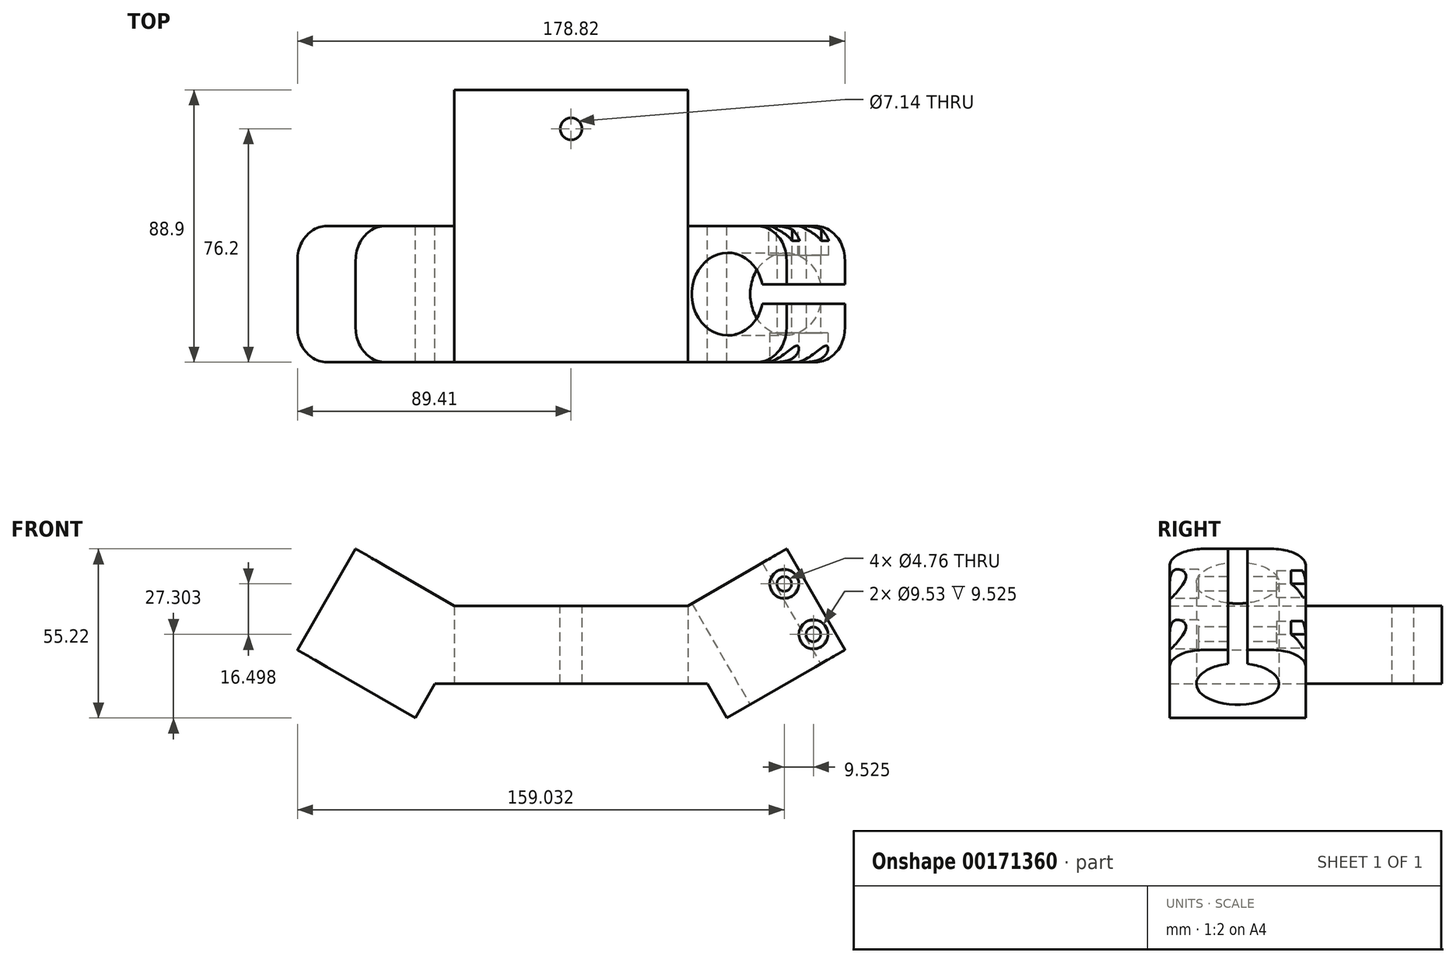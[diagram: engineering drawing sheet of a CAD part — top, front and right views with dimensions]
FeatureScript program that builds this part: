
annotation { "Feature Type Name" : "Feature", "Feature Type Description" : "" }
export const myFeature = defineFeature(function(context is Context, id is Id, definition is map)
    precondition{}
    {
        {
            var Q0;
            Q0=qCreatedBy(makeId("Front.planeOp"),FACE);
            var sketch = newSketch(context, id + "F0", { "sketchPlane" : qUnion([Q0])});
            skLineSegment(sketch, "E0", {"start": v(0, 0) * mm, "end": v(38.1, 0) * mm});
            skLineSegment(sketch, "E1", {"start": v(38.1, 0) * mm, "end": v(70.36, 18.62) * mm});
            skLineSegment(sketch, "E2", {"start": v(70.36, 18.62) * mm, "end": v(89.4, -14.37) * mm});
            skLineSegment(sketch, "E3", {"start": v(89.4, -14.37) * mm, "end": v(50.91, -36.6) * mm});
            skLineSegment(sketch, "E4", {"start": v(50.91, -36.6) * mm, "end": v(44.45, -25.4) * mm});
            skLineSegment(sketch, "E5", {"start": v(44.45, -25.4) * mm, "end": v(0, -25.4) * mm});
            skLineSegment(sketch, "E6.MirrorCS", {"start": v(-44.45, -25.4) * mm, "end": v(0, -25.4) * mm});
            skLineSegment(sketch, "E7.MirrorCS", {"start": v(0, 0) * mm, "end": v(-38.1, 0) * mm});
            skLineSegment(sketch, "E8.MirrorCS", {"start": v(-50.91, -36.6) * mm, "end": v(-44.45, -25.4) * mm});
            skLineSegment(sketch, "E9.MirrorCS", {"start": v(-70.36, 18.62) * mm, "end": v(-89.4, -14.37) * mm});
            skLineSegment(sketch, "E10.MirrorCS", {"start": v(-89.4, -14.37) * mm, "end": v(-50.91, -36.6) * mm});
            skLineSegment(sketch, "E11.MirrorCS", {"start": v(-38.1, 0) * mm, "end": v(-70.36, 18.62) * mm});
            skSolve(sketch);
        }
        {
            var Q0;
            Q0=makeQuery(id+"F0.imprint","IMPRINT",FACE,{"disambiguationData":[TD([[makeQuery(id+"F0.imprint","IMPRINT",EDGE,{"derivedFrom":sQuery(id+"F0.wireOp",EDGE,"E0")}),-1.0]])]});
            extrude(context, id + "F1", {"entities" : qUnion([Q0]), "depth" : 44.45 * mm});
        }
        {
            var Q0;
            Q0=makeQuery(id+"F1.opExtrude","SWEPT_FACE",FACE,{"disambiguationData":[OSD([sQuery(id+"F0.wireOp",EDGE,"E3")])]});
            var sketch = newSketch(context, id + "F2", { "sketchPlane" : qUnion([Q0])});
            skCircle(sketch, "E12", {"center": v(48.02, 22.22) * mm, "radius": 13.5 * mm});
            skSolve(sketch);
        }
        {
            var Q0;
            Q0=makeQuery(id+"F2.imprint","IMPRINT",FACE,{"disambiguationData":[TD([[makeQuery(id+"F2.imprint","IMPRINT",EDGE,{"derivedFrom":sQuery(id+"F2.wireOp",EDGE,"E12")}),1.0]])]});
            extrude(context, id + "F3", {"entities" : qUnion([Q0]), "operationType" : NewBodyOperationType.REMOVE, "endBound" : BoundingType.UP_TO_NEXT, "oppositeDirection" : true, "depth" : 25.4 * mm});
        }
        {
            var Q0;
            Q0=makeQuery(id+"F1.opExtrude","SWEPT_FACE",FACE,{"disambiguationData":[OSD([sQuery(id+"F0.wireOp",EDGE,"E2")])]});
            var sketch = newSketch(context, id + "F4", { "sketchPlane" : qUnion([Q0])});
            skLineSegment(sketch, "E13.bottom", {"start": v(-25.4, -19.05) * mm, "end": v(-19.05, -19.05) * mm});
            skLineSegment(sketch, "E13.top", {"start": v(-25.4, -57.15) * mm, "end": v(-19.05, -57.15) * mm});
            skLineSegment(sketch, "E13.left", {"start": v(-25.4, -19.05) * mm, "end": v(-25.4, -57.15) * mm});
            skLineSegment(sketch, "E13.right", {"start": v(-19.05, -19.05) * mm, "end": v(-19.05, -57.15) * mm});
            skLineSegment(sketch, "E14", {"start": v(-22.23, -19.05) * mm, "end": v(-22.23, -57.15) * mm, "construction": true});
            skSolve(sketch);
        }
        {
            var Q0;
            Q0=makeQuery(id+"F4.imprint","IMPRINT",FACE,{"disambiguationData":[TD([[makeQuery(id+"F4.imprint","IMPRINT",EDGE,{"derivedFrom":sQuery(id+"F4.wireOp",EDGE,"E13.bottom")}),-1.0]])]});
            extrude(context, id + "F5", {"entities" : qUnion([Q0]), "operationType" : NewBodyOperationType.REMOVE, "endBound" : BoundingType.UP_TO_NEXT, "oppositeDirection" : true, "depth" : 25.4 * mm});
        }
        {
            var Q0;
            Q0=makeQuery(id+"F1.opExtrude","CAP_FACE",FACE,{"disambiguationData":[OSD([sQuery(id+"F0.wireOp",EDGE,"E0"),sQuery(id+"F0.wireOp",EDGE,"E1"),sQuery(id+"F0.wireOp",EDGE,"E2"),sQuery(id+"F0.wireOp",EDGE,"E3"),sQuery(id+"F0.wireOp",EDGE,"E4"),sQuery(id+"F0.wireOp",EDGE,"E5"),sQuery(id+"F0.wireOp",EDGE,"E6.MirrorCS"),sQuery(id+"F0.wireOp",EDGE,"E7.MirrorCS"),sQuery(id+"F0.wireOp",EDGE,"E8.MirrorCS"),sQuery(id+"F0.wireOp",EDGE,"E9.MirrorCS"),sQuery(id+"F0.wireOp",EDGE,"E10.MirrorCS"),sQuery(id+"F0.wireOp",EDGE,"E11.MirrorCS")])],"isStart":false});
            var sketch = newSketch(context, id + "F6", { "sketchPlane" : qUnion([Q0])});
            skLineSegment(sketch, "E15", {"start": v(64.86, 15.45) * mm, "end": v(83.9, -17.55) * mm, "construction": true});
            skPoint(sketch, "E16", {"position": v(69.62, 7.2) * mm});
            skPoint(sketch, "E17", {"position": v(79.15, -9.3) * mm});
            skSolve(sketch);
        }
        {
            var Q0;
            Q0=sQuery(id+"F6.wireOp",VERTEX,"E16");
            var Q1;
            Q1=sQuery(id+"F6.wireOp",VERTEX,"E17");
            var Q2;
            Q2=makeQuery(id+"F1.opExtrude","SWEPT_BODY",BODY,{"disambiguationData":[OSD([sQuery(id+"F0.wireOp",EDGE,"E0"),sQuery(id+"F0.wireOp",EDGE,"E1"),sQuery(id+"F0.wireOp",EDGE,"E2"),sQuery(id+"F0.wireOp",EDGE,"E3"),sQuery(id+"F0.wireOp",EDGE,"E4"),sQuery(id+"F0.wireOp",EDGE,"E5"),sQuery(id+"F0.wireOp",EDGE,"E6.MirrorCS"),sQuery(id+"F0.wireOp",EDGE,"E7.MirrorCS"),sQuery(id+"F0.wireOp",EDGE,"E8.MirrorCS"),sQuery(id+"F0.wireOp",EDGE,"E9.MirrorCS"),sQuery(id+"F0.wireOp",EDGE,"E10.MirrorCS"),sQuery(id+"F0.wireOp",EDGE,"E11.MirrorCS")])]});
            hole(context, id + "F7", {"style" : HoleStyle.C_BORE, "endStyle" : HoleEndStyle.THROUGH, "holeDiameter" : 4.76 * mm, "cBoreDiameter" : 9.52 * mm, "cBoreDepth" : 9.52 * mm, "locations" : qUnion([Q0, Q1]), "scope" : qUnion([Q2]), "isTappedThrough" : true});
        }
        {
            var Q0;
            Q0=makeQuery(id+"F1.opExtrude","CAP_FACE",FACE,{"disambiguationData":[OSD([sQuery(id+"F0.wireOp",EDGE,"E0"),sQuery(id+"F0.wireOp",EDGE,"E1"),sQuery(id+"F0.wireOp",EDGE,"E2"),sQuery(id+"F0.wireOp",EDGE,"E3"),sQuery(id+"F0.wireOp",EDGE,"E4"),sQuery(id+"F0.wireOp",EDGE,"E5"),sQuery(id+"F0.wireOp",EDGE,"E6.MirrorCS"),sQuery(id+"F0.wireOp",EDGE,"E7.MirrorCS"),sQuery(id+"F0.wireOp",EDGE,"E8.MirrorCS"),sQuery(id+"F0.wireOp",EDGE,"E9.MirrorCS"),sQuery(id+"F0.wireOp",EDGE,"E10.MirrorCS"),sQuery(id+"F0.wireOp",EDGE,"E11.MirrorCS")])],"isStart":true});
            var sketch = newSketch(context, id + "F8", { "sketchPlane" : qUnion([Q0])});
            skCircle(sketch, "E18.cCircle", {"center": v(-69.62, 7.2) * mm, "radius": 4.37 * mm, "construction": true});
            skLineSegment(sketch, "E18.0", {"start": v(-67.1, 11.57) * mm, "end": v(-64.58, 7.2) * mm});
            skLineSegment(sketch, "E18.1", {"start": v(-64.58, 7.2) * mm, "end": v(-67.1, 2.84) * mm});
            skLineSegment(sketch, "E18.2", {"start": v(-67.1, 2.84) * mm, "end": v(-72.14, 2.84) * mm});
            skLineSegment(sketch, "E18.3", {"start": v(-72.14, 2.84) * mm, "end": v(-74.66, 7.2) * mm});
            skLineSegment(sketch, "E18.4", {"start": v(-74.66, 7.2) * mm, "end": v(-72.14, 11.57) * mm});
            skLineSegment(sketch, "E18.5", {"start": v(-72.14, 11.57) * mm, "end": v(-67.1, 11.57) * mm});
            skPoint(sketch, "E18.0.midPoint", {"position": v(-65.84, 9.38) * mm});
            skCircle(sketch, "E19.cCircle", {"center": v(-79.15, -9.3) * mm, "radius": 4.37 * mm, "construction": true});
            skLineSegment(sketch, "E19.0", {"start": v(-74.1, -9.3) * mm, "end": v(-76.63, -13.66) * mm});
            skLineSegment(sketch, "E19.1", {"start": v(-76.63, -13.66) * mm, "end": v(-81.67, -13.66) * mm});
            skLineSegment(sketch, "E19.2", {"start": v(-81.67, -13.66) * mm, "end": v(-84.19, -9.3) * mm});
            skLineSegment(sketch, "E19.3", {"start": v(-84.19, -9.3) * mm, "end": v(-81.67, -4.93) * mm});
            skLineSegment(sketch, "E19.4", {"start": v(-81.67, -4.93) * mm, "end": v(-76.63, -4.93) * mm});
            skLineSegment(sketch, "E19.5", {"start": v(-76.63, -4.93) * mm, "end": v(-74.1, -9.3) * mm});
            skPoint(sketch, "E19.0.midPoint", {"position": v(-75.37, -11.48) * mm});
            skSolve(sketch);
        }
        {
            var Q0;
            Q0=makeQuery(id+"F8.imprint","IMPRINT",FACE,{"disambiguationData":[TD([[makeQuery(id+"F8.imprint","IMPRINT",EDGE,{"derivedFrom":sQuery(id+"F8.wireOp",EDGE,"E18.0")}),-1.0]])]});
            var Q1;
            Q1=makeQuery(id+"F8.imprint","IMPRINT",FACE,{"disambiguationData":[TD([[makeQuery(id+"F8.imprint","IMPRINT",EDGE,{"derivedFrom":sQuery(id+"F8.wireOp",EDGE,"E19.0")}),-1.0]])]});
            extrude(context, id + "F9", {"entities" : qUnion([Q0, Q1]), "operationType" : NewBodyOperationType.REMOVE, "oppositeDirection" : true, "depth" : 9.52 * mm});
        }
        {
            var Q0;
            Q0=makeQuery(id+"F1.opExtrude","CAP_EDGE",EDGE,{"disambiguationData":[OSD([sQuery(id+"F0.wireOp",EDGE,"E2")])],"isStart":false});
            var Q1;
            Q1=makeQuery(id+"F1.opExtrude","CAP_EDGE",EDGE,{"disambiguationData":[OSD([sQuery(id+"F0.wireOp",EDGE,"E2")])],"isStart":true});
            fillet(context, id + "F10", {"entities" : qUnion([Q0, Q1]), "radius" : 11.1 * mm, "tangentPropagation" : true, "allowEdgeOverflow" : false});
        }
        {
            var Q0;
            Q0=makeQuery(id+"F1.opExtrude","CAP_FACE",FACE,{"disambiguationData":[OSD([sQuery(id+"F0.wireOp",EDGE,"E0"),sQuery(id+"F0.wireOp",EDGE,"E1"),sQuery(id+"F0.wireOp",EDGE,"E2"),sQuery(id+"F0.wireOp",EDGE,"E3"),sQuery(id+"F0.wireOp",EDGE,"E4"),sQuery(id+"F0.wireOp",EDGE,"E5"),sQuery(id+"F0.wireOp",EDGE,"E6.MirrorCS"),sQuery(id+"F0.wireOp",EDGE,"E7.MirrorCS"),sQuery(id+"F0.wireOp",EDGE,"E8.MirrorCS"),sQuery(id+"F0.wireOp",EDGE,"E9.MirrorCS"),sQuery(id+"F0.wireOp",EDGE,"E10.MirrorCS"),sQuery(id+"F0.wireOp",EDGE,"E11.MirrorCS")])],"isStart":true});
            var sketch = newSketch(context, id + "F11", { "sketchPlane" : qUnion([Q0])});
            skLineSegment(sketch, "E20.bottom", {"start": v(-38.1, 0) * mm, "end": v(38.1, 0) * mm});
            skLineSegment(sketch, "E20.top", {"start": v(-38.1, -25.4) * mm, "end": v(38.1, -25.4) * mm});
            skLineSegment(sketch, "E20.left", {"start": v(-38.1, 0) * mm, "end": v(-38.1, -25.4) * mm});
            skLineSegment(sketch, "E20.right", {"start": v(38.1, 0) * mm, "end": v(38.1, -25.4) * mm});
            skSolve(sketch);
        }
        {
            var Q0;
            Q0=makeQuery(id+"F11.imprint","IMPRINT",FACE,{"disambiguationData":[TD([[makeQuery(id+"F11.imprint","IMPRINT",EDGE,{"derivedFrom":sQuery(id+"F11.wireOp",EDGE,"E20.bottom")}),1.0]])]});
            extrude(context, id + "F12", {"entities" : qUnion([Q0]), "operationType" : NewBodyOperationType.ADD, "depth" : 44.45 * mm});
        }
        {
            var Q0;
            Q0=makeQuery(id+"F12.boolean.opBoolean","MERGE",FACE,{"derivedFrom":[makeQuery(id+"F1.opExtrude","SWEPT_FACE",FACE,{"disambiguationData":[OSD([sQuery(id+"F0.wireOp",EDGE,"E0"),sQuery(id+"F0.wireOp",EDGE,"E7.MirrorCS")])]}),makeQuery(id+"F12.opExtrude","SWEPT_FACE",FACE,{"disambiguationData":[OSD([sQuery(id+"F11.wireOp",EDGE,"E20.bottom")])]})]});
            var sketch = newSketch(context, id + "F13", { "sketchPlane" : qUnion([Q0])});
            skPoint(sketch, "E21", {"position": v(0, 31.75) * mm});
            skSolve(sketch);
        }
        {
            var Q0;
            Q0=sQuery(id+"F13.wireOp",VERTEX,"E21");
            var Q1;
            Q1=makeQuery(id+"F1.opExtrude","SWEPT_BODY",BODY,{"disambiguationData":[OSD([sQuery(id+"F0.wireOp",EDGE,"E0"),sQuery(id+"F0.wireOp",EDGE,"E1"),sQuery(id+"F0.wireOp",EDGE,"E2"),sQuery(id+"F0.wireOp",EDGE,"E3"),sQuery(id+"F0.wireOp",EDGE,"E4"),sQuery(id+"F0.wireOp",EDGE,"E5"),sQuery(id+"F0.wireOp",EDGE,"E6.MirrorCS"),sQuery(id+"F0.wireOp",EDGE,"E7.MirrorCS"),sQuery(id+"F0.wireOp",EDGE,"E8.MirrorCS"),sQuery(id+"F0.wireOp",EDGE,"E9.MirrorCS"),sQuery(id+"F0.wireOp",EDGE,"E10.MirrorCS"),sQuery(id+"F0.wireOp",EDGE,"E11.MirrorCS")])]});
            hole(context, id + "F14", {"style" : HoleStyle.SIMPLE, "endStyle" : HoleEndStyle.THROUGH, "holeDiameter" : 7.14 * mm, "locations" : qUnion([Q0]), "scope" : qUnion([Q1]), "isTappedThrough" : true});
        }
        {
            var Q0;
            Q0=makeQuery(id+"F1.opExtrude","CAP_EDGE",EDGE,{"disambiguationData":[OSD([sQuery(id+"F0.wireOp",EDGE,"E9.MirrorCS")])],"isStart":true});
            var Q1;
            Q1=makeQuery(id+"F1.opExtrude","CAP_EDGE",EDGE,{"disambiguationData":[OSD([sQuery(id+"F0.wireOp",EDGE,"E9.MirrorCS")])],"isStart":false});
            fillet(context, id + "F15", {"entities" : qUnion([Q0, Q1]), "radius" : 11.1 * mm, "tangentPropagation" : true, "allowEdgeOverflow" : false});
        }
    });
